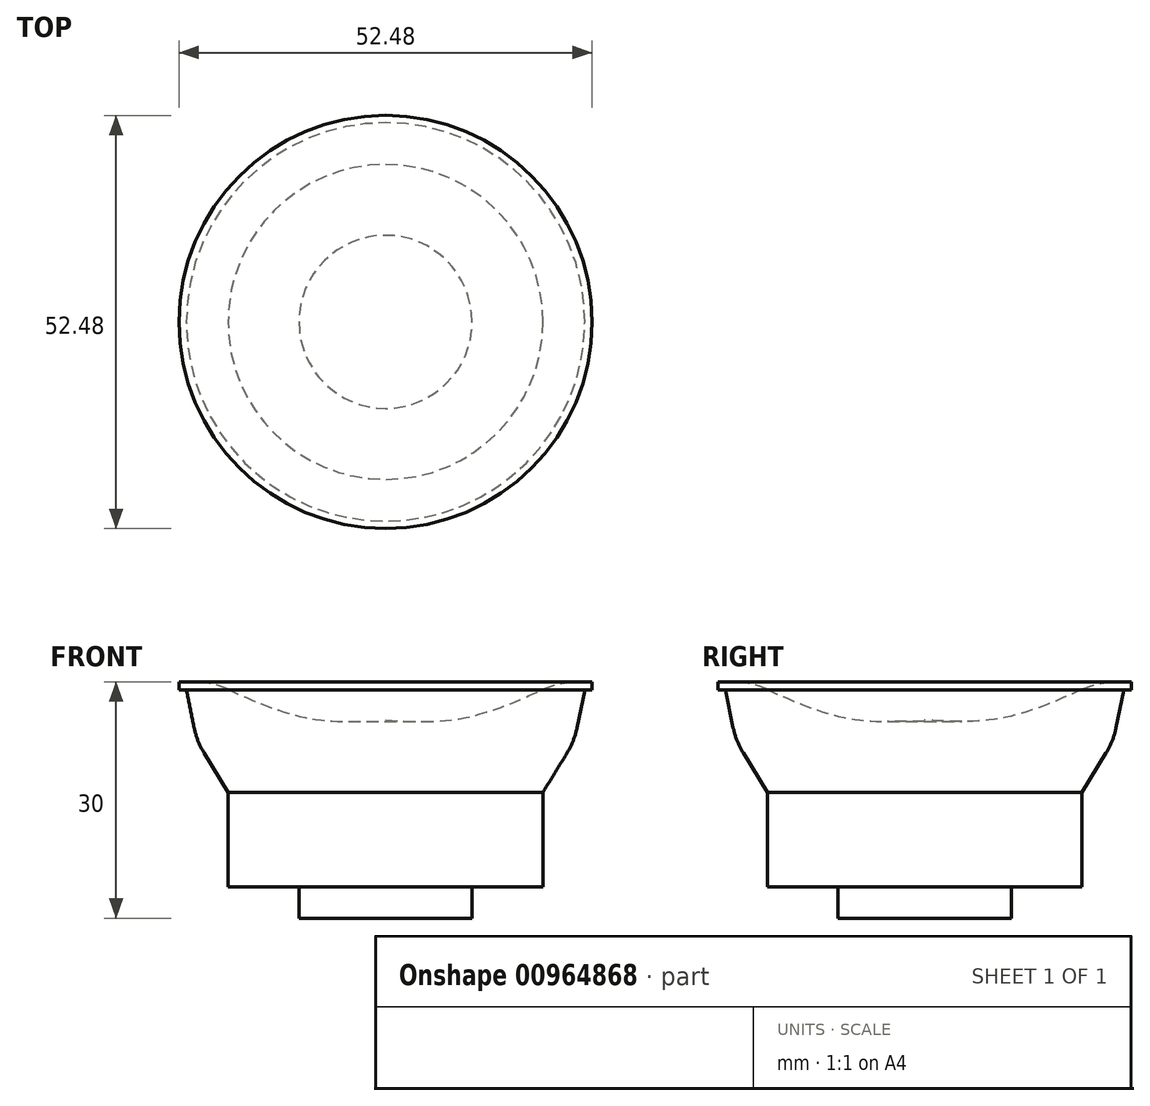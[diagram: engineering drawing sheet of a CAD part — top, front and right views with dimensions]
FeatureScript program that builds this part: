
annotation { "Feature Type Name" : "Feature", "Feature Type Description" : "" }
export const myFeature = defineFeature(function(context is Context, id is Id, definition is map)
    precondition{}
    {
        {
            var Q0;
            Q0=qCreatedBy(makeId("Top.planeOp"),FACE);
            var sketch = newSketch(context, id + "F0", { "sketchPlane" : qUnion([Q0])});
            skCircle(sketch, "E0", {"center": v(0, 0) * mm, "radius": 11 * mm});
            skSolve(sketch);
        }
        {
            var Q0;
            Q0=makeQuery(id+"F0.imprint","IMPRINT",FACE,{"disambiguationData":[TD([[makeQuery(id+"F0.imprint","IMPRINT",EDGE,{"derivedFrom":sQuery(id+"F0.wireOp",EDGE,"E0")}),1.0]])]});
            extrude(context, id + "F1", {"entities" : qUnion([Q0]), "depth" : 4 * mm});
        }
        {
            var Q0;
            Q0=makeQuery(id+"F1.opExtrude","CAP_FACE",FACE,{"disambiguationData":[OSD([sQuery(id+"F0.wireOp",EDGE,"E0")])],"isStart":false});
            var sketch = newSketch(context, id + "F2", { "sketchPlane" : qUnion([Q0])});
            skCircle(sketch, "E1", {"center": v(0, 0) * mm, "radius": 20 * mm});
            skSolve(sketch);
        }
        {
            var Q0;
            Q0=makeQuery(id+"F2.imprint","IMPRINT",FACE,{"disambiguationData":[TD([[makeQuery(id+"F2.imprint","IMPRINT",EDGE,{"derivedFrom":sQuery(id+"F2.wireOp",EDGE,"E1")}),1.0]])]});
            var Q1;
            Q1=makeQuery(id+"F2.imprint","IMPRINT",FACE,{"disambiguationData":[TD([[makeQuery(id+"F2.imprint","IMPRINT",EDGE,{"derivedFrom":makeQuery(id+"F1.opExtrude","CAP_EDGE",EDGE,{"disambiguationData":[OSD([sQuery(id+"F0.wireOp",EDGE,"E0")])],"isStart":false})}),1.0]])]});
            extrude(context, id + "F3", {"entities" : qUnion([Q0, Q1]), "operationType" : NewBodyOperationType.ADD, "depth" : 12 * mm});
        }
        {
            var Q0;
            Q0=qCreatedBy(makeId("Front.planeOp"),FACE);
            var sketch = newSketch(context, id + "F4", { "sketchPlane" : qUnion([Q0])});
            skLineSegment(sketch, "E2", {"start": v(0, 0) * mm, "end": v(0, 43.46) * mm, "construction": true});
            skLineSegment(sketch, "E3", {"start": v(24.24, 30) * mm, "end": v(26.24, 30) * mm});
            skLineSegment(sketch, "E4", {"start": v(26.24, 30) * mm, "end": v(26.24, 29) * mm});
            skLineSegment(sketch, "E5", {"start": v(23.05, 20.97) * mm, "end": v(20, 16) * mm});
            skLineSegment(sketch, "E6", {"start": v(20, 16) * mm, "end": v(0, 16) * mm});
            skPoint(sketch, "E7.visualSharp", {"position": v(26.24, 26.18) * mm});
            skFitSpline(sketch, "E8", {"points": [v(0, 25.15) * mm, v(10.04, 25.44) * mm, v(22.04, 30) * mm], "startDerivative": vector(21.1, -1.24) * mm, "endDerivative": vector(22.93, 10.7) * mm});
            skPoint(sketch, "E9.newPointB", {"position": v(0.14, 30) * mm});
            skArc(sketch, "E9.filletArc", {"start": v(24.24, 30) * mm, "mid": v(22.1, 29.77) * mm, "end": v(20.07, 29.09) * mm});
            skLineSegment(sketch, "E10", {"start": v(0, 25.15) * mm, "end": v(0, 16) * mm});
            skLineSegment(sketch, "E11", {"start": v(26.24, 29) * mm, "end": v(25.3, 29) * mm});
            skLineSegment(sketch, "E12", {"start": v(25.3, 29) * mm, "end": v(24.32, 24.19) * mm});
            skArc(sketch, "E13.filletArc", {"start": v(23.05, 20.97) * mm, "mid": v(23.82, 22.52) * mm, "end": v(24.32, 24.19) * mm});
            skSolve(sketch);
        }
        {
            var Q0;
            Q0=qSketchRegion(id+"F4",true);
            var Q1;
            Q1=sQuery(id+"F4.wireOp",EDGE,"E2");
            revolve(context, id + "F5", {"operationType" : NewBodyOperationType.ADD, "entities" : qUnion([Q0]), "axis" : qUnion([Q1]), "revolveType" : RevolveType.FULL});
        }
    });
